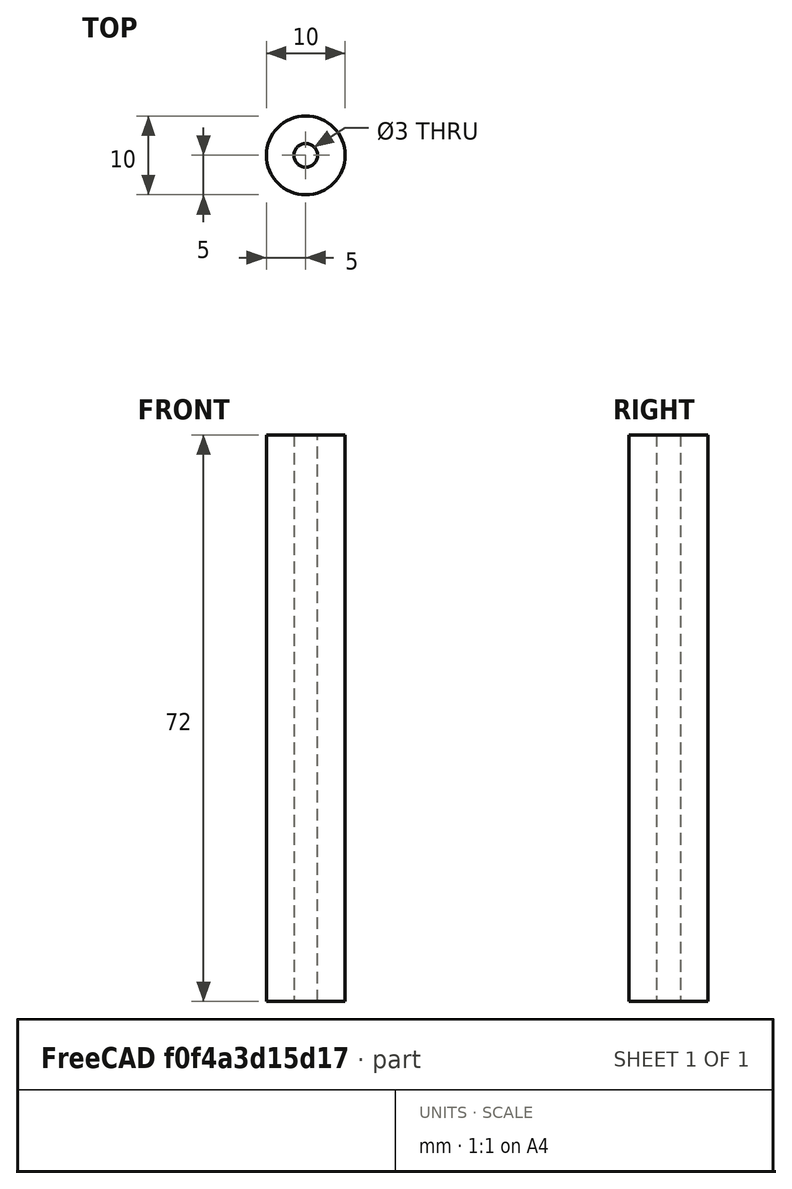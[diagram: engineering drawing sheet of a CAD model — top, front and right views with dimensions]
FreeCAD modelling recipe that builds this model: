
FCSTD DOCUMENT  (FreeCAD 1.0R39109 (Git))
Label: bodySpacer
License: All rights reserved
LicenseURL: https://en.wikipedia.org/wiki/All_rights_reserved
objects: Sketcher::SketchObject×1, PartDesign::Pad×1, PartDesign::Body×1
note: 6 computed .brp shape members not serialized (recipe doc carries the construction recipe); baked Part::Feature solids carry a one-line shape summary decoded from their .brp

FEATURE [Sketcher::SketchObject] Sketch
  ArcFitTolerance = 1e-06
  AttachmentSupport = -> [XY_Plane]
  FullyConstrained = true
  MakeInternals = false
  MapMode = 5
  sketch-geometry (2):
    g0: Circle CenterX=0 CenterY=0 CenterZ=0 NormalX=0 NormalY=0 NormalZ=1 AngleXU=0 Radius=1.5
    g1: Circle CenterX=0 CenterY=0 CenterZ=0 NormalX=0 NormalY=0 NormalZ=1 AngleXU=0 Radius=5
  constraints (4):
    c: Coincident(g0,g-1)
    c: Coincident(g1,g0)
    c: Diameter(g0) = 3
    c: Distance(g0,g1) = 3.5
FEATURE [PartDesign::Pad] Pad
  Direction = (0,0,1)
  Length = 72
  Length2 = 10
  Profile = -> Sketch
  ReferenceAxis = -> Sketch [N_Axis]
  Refine = true
  Suppressed = false
  Type = 0
FEATURE [PartDesign::Body] Body
  AllowCompound = false
  Group = -> [Sketch,Pad]
  Origin = -> Origin
  Tip = -> Pad
